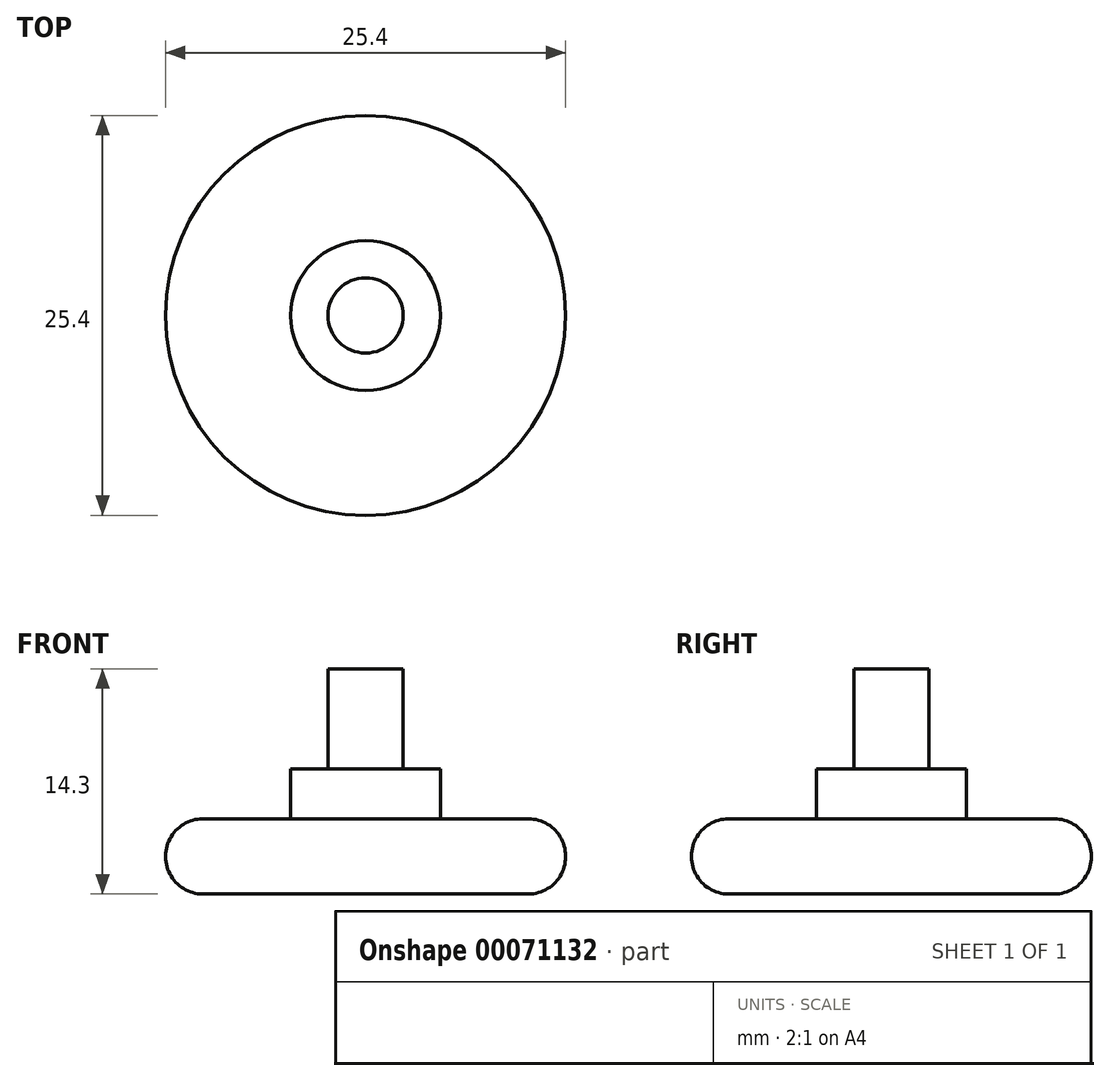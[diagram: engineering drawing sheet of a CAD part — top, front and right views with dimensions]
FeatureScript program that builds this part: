
annotation { "Feature Type Name" : "Feature", "Feature Type Description" : "" }
export const myFeature = defineFeature(function(context is Context, id is Id, definition is map)
    precondition{}
    {
        {
            var Q0;
            Q0=qCreatedBy(makeId("Front.planeOp"),FACE);
            var sketch = newSketch(context, id + "F0", { "sketchPlane" : qUnion([Q0])});
            skLineSegment(sketch, "E0.bottom", {"start": v(9.4, 5.76) * mm, "end": v(22.1, 5.76) * mm});
            skLineSegment(sketch, "E0.top", {"start": v(9.4, 0.98) * mm, "end": v(22.1, 0.98) * mm});
            skLineSegment(sketch, "E0.left", {"start": v(9.4, 5.76) * mm, "end": v(9.4, 0.98) * mm});
            skLineSegment(sketch, "E0.right", {"start": v(22.1, 5.76) * mm, "end": v(22.1, 0.98) * mm});
            skSolve(sketch);
        }
        {
            var Q0;
            Q0=makeQuery(id+"F0.imprint","IMPRINT",FACE,{"disambiguationData":[TD([[makeQuery(id+"F0.imprint","IMPRINT",EDGE,{"derivedFrom":sQuery(id+"F0.wireOp",EDGE,"E0.bottom")}),-1.0]])]});
            var Q1;
            Q1=sQuery(id+"F0.wireOp",EDGE,"E0.left");
            revolve(context, id + "F1", {"entities" : qUnion([Q0]), "axis" : qUnion([Q1]), "revolveType" : RevolveType.FULL});
        }
        {
            var Q0;
            Q0=makeQuery(id+"F1.opRevolve","SWEPT_EDGE",EDGE,{"disambiguationData":[OSD([sQuery(id+"F0.wireOp",EDGE,"E0.bottom"),sQuery(id+"F0.wireOp",EDGE,"E0.right")])]});
            var Q1;
            Q1=makeQuery(id+"F1.opRevolve","SWEPT_EDGE",EDGE,{"disambiguationData":[OSD([sQuery(id+"F0.wireOp",EDGE,"E0.top"),sQuery(id+"F0.wireOp",EDGE,"E0.right")])]});
            fillet(context, id + "F2", {"entities" : qUnion([Q0, Q1]), "radius" : 2.36 * mm, "tangentPropagation" : true, "allowEdgeOverflow" : false});
        }
        {
            var Q0;
            Q0=makeQuery(id+"F1.opRevolve","SWEPT_FACE",FACE,{"disambiguationData":[OSD([sQuery(id+"F0.wireOp",EDGE,"E0.bottom")])]});
            var sketch = newSketch(context, id + "F3", { "sketchPlane" : qUnion([Q0])});
            skCircle(sketch, "E1", {"center": v(9.4, 0) * mm, "radius": 4.76 * mm});
            skSolve(sketch);
        }
        {
            var Q0;
            Q0 = qSketchRegion(id + "F3", true);
            extrude(context, id + "F4", {"entities" : qUnion([Q0]), "operationType" : NewBodyOperationType.ADD, "depth" : 3.17 * mm});
        }
        {
            var Q0;
            Q0=makeQuery(id+"F1.opRevolve","SWEPT_FACE",FACE,{"disambiguationData":[OSD([sQuery(id+"F0.wireOp",EDGE,"E0.bottom")])]});
            var sketch = newSketch(context, id + "F5", { "sketchPlane" : qUnion([Q0])});
            skCircle(sketch, "E2", {"center": v(9.4, 0) * mm, "radius": 2.39 * mm});
            skSolve(sketch);
        }
        {
            var Q0;
            Q0 = qSketchRegion(id + "F5", true);
            extrude(context, id + "F6", {"entities" : qUnion([Q0]), "operationType" : NewBodyOperationType.ADD, "depth" : 9.52 * mm});
        }
    });
